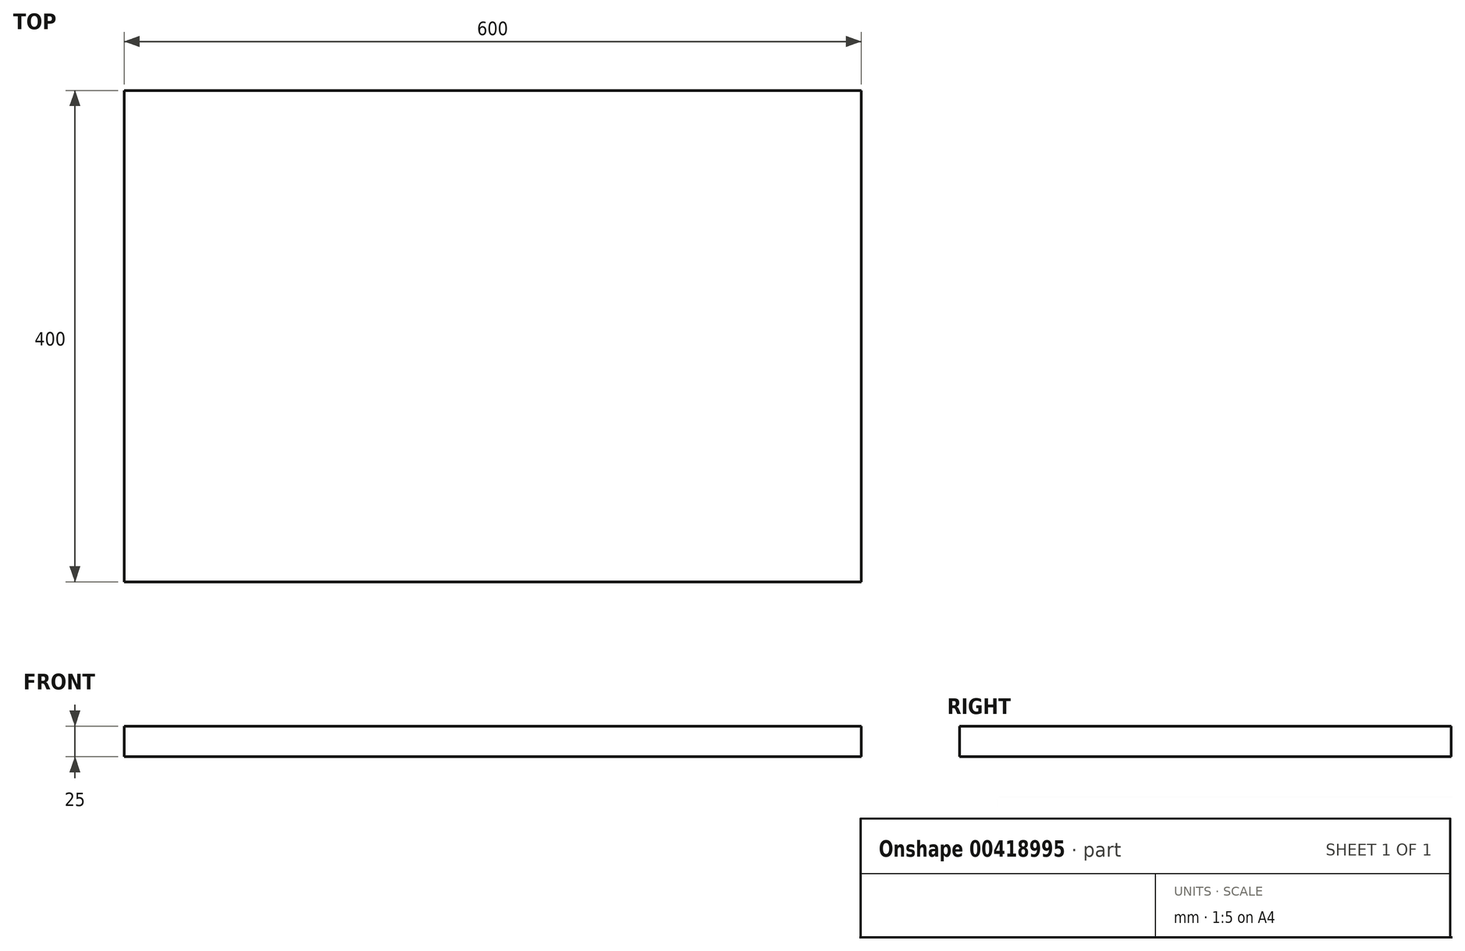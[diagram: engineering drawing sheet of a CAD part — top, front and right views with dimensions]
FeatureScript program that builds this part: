
annotation { "Feature Type Name" : "Feature", "Feature Type Description" : "" }
export const myFeature = defineFeature(function(context is Context, id is Id, definition is map)
    precondition{}
    {
        {
            var Q0;
            Q0=qCreatedBy(makeId("Top.planeOp"),FACE);
            var sketch = newSketch(context, id + "F0", { "sketchPlane" : qUnion([Q0])});
            skLineSegment(sketch, "E0.bottom", {"start": v(300, 200) * mm, "end": v(-300, 200) * mm});
            skLineSegment(sketch, "E0.top", {"start": v(300, -200) * mm, "end": v(-300, -200) * mm});
            skLineSegment(sketch, "E0.left", {"start": v(300, 200) * mm, "end": v(300, -200) * mm});
            skLineSegment(sketch, "E0.right", {"start": v(-300, 200) * mm, "end": v(-300, -200) * mm});
            skPoint(sketch, "E0.middle", {"position": v(0, 0) * mm});
            skSolve(sketch);
        }
        {
            var Q0;
            Q0 = qSketchRegion(id + "F0", true);
            extrude(context, id + "F1", {"entities" : qUnion([Q0]), "depth" : 25 * mm, "offsetDistance" : 25 * mm});
        }
    });
